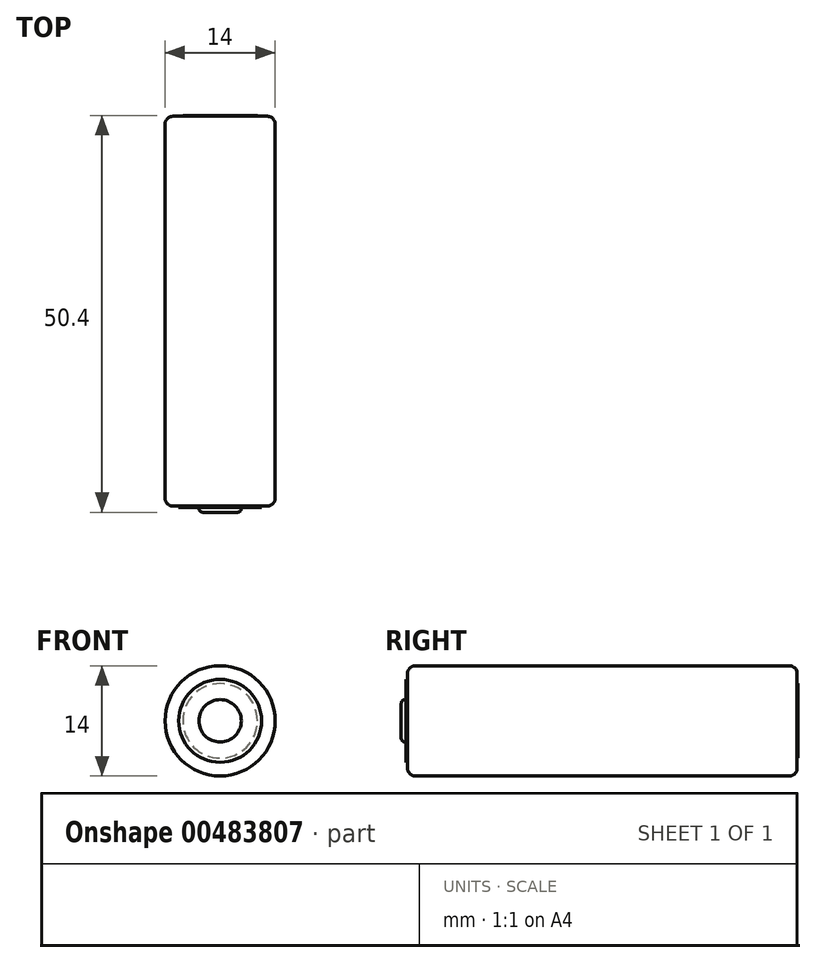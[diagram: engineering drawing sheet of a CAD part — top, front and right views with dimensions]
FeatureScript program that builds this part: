
annotation { "Feature Type Name" : "Feature", "Feature Type Description" : "" }
export const myFeature = defineFeature(function(context is Context, id is Id, definition is map)
    precondition{}
    {
        {
            var Q0;
            Q0=qCreatedBy(makeId("Front.planeOp"),FACE);
            var sketch = newSketch(context, id + "F0", { "sketchPlane" : qUnion([Q0])});
            skCircle(sketch, "E0", {"center": v(0, 0) * mm, "radius": 7 * mm});
            skSolve(sketch);
        }
        {
            var Q0;
            Q0=qSketchRegion(id+"F0",true);
            extrude(context, id + "F1", {"entities" : qUnion([Q0]), "depth" : 49.5 * mm});
        }
        {
            var Q0;
            Q0=makeQuery(id+"F1.opExtrude","CAP_FACE",FACE,{"disambiguationData":[OSD([sQuery(id+"F0.wireOp",EDGE,"E0")])],"isStart":false});
            var sketch = newSketch(context, id + "F2", { "sketchPlane" : qUnion([Q0])});
            skCircle(sketch, "E1", {"center": v(0, 0) * mm, "radius": 5.27 * mm});
            skSolve(sketch);
        }
        {
            var Q0;
            Q0=qSketchRegion(id+"F2",true);
            extrude(context, id + "F3", {"entities" : qUnion([Q0]), "depth" : .2 * mm});
        }
        {
            var Q0;
            Q0=makeQuery(id+"F1.opExtrude","CAP_EDGE",EDGE,{"disambiguationData":[OSD([sQuery(id+"F0.wireOp",EDGE,"E0")])],"isStart":false});
            var Q1;
            Q1=makeQuery(id+"F1.opExtrude","CAP_EDGE",EDGE,{"disambiguationData":[OSD([sQuery(id+"F0.wireOp",EDGE,"E0")])],"isStart":true});
            fillet(context, id + "F4", {"entities" : qUnion([Q0, Q1]), "radius" : 1 * mm, "tangentPropagation" : true, "allowEdgeOverflow" : false});
        }
        {
            var Q0;
            Q0=makeQuery(id+"F3.opExtrude","CAP_FACE",FACE,{"disambiguationData":[OSD([sQuery(id+"F2.wireOp",EDGE,"E1")])],"isStart":false});
            var sketch = newSketch(context, id + "F5", { "sketchPlane" : qUnion([Q0])});
            skCircle(sketch, "E2", {"center": v(0, 0) * mm, "radius": 2.7 * mm});
            skSolve(sketch);
        }
        {
            var Q0;
            Q0=qSketchRegion(id+"F5",true);
            extrude(context, id + "F6", {"entities" : qUnion([Q0]), "operationType" : NewBodyOperationType.ADD, "depth" : .6 * mm});
        }
        {
            var Q0;
            Q0=makeQuery(id+"F6.opExtrude","CAP_EDGE",EDGE,{"disambiguationData":[OSD([sQuery(id+"F5.wireOp",EDGE,"E2")])],"isStart":false});
            fillet(context, id + "F7", {"entities" : qUnion([Q0]), "radius" : .5 * mm, "tangentPropagation" : true, "allowEdgeOverflow" : false});
        }
        {
            var Q0;
            Q0=makeQuery(id+"F1.opExtrude","CAP_FACE",FACE,{"disambiguationData":[OSD([sQuery(id+"F0.wireOp",EDGE,"E0")])],"isStart":true});
            var sketch = newSketch(context, id + "F8", { "sketchPlane" : qUnion([Q0])});
            skCircle(sketch, "E3", {"center": v(0, 0) * mm, "radius": 4.73 * mm});
            skSolve(sketch);
        }
        {
            var Q0;
            Q0=qSketchRegion(id+"F8",true);
            extrude(context, id + "F9", {"entities" : qUnion([Q0]), "depth" : .1 * mm});
        }
    });
